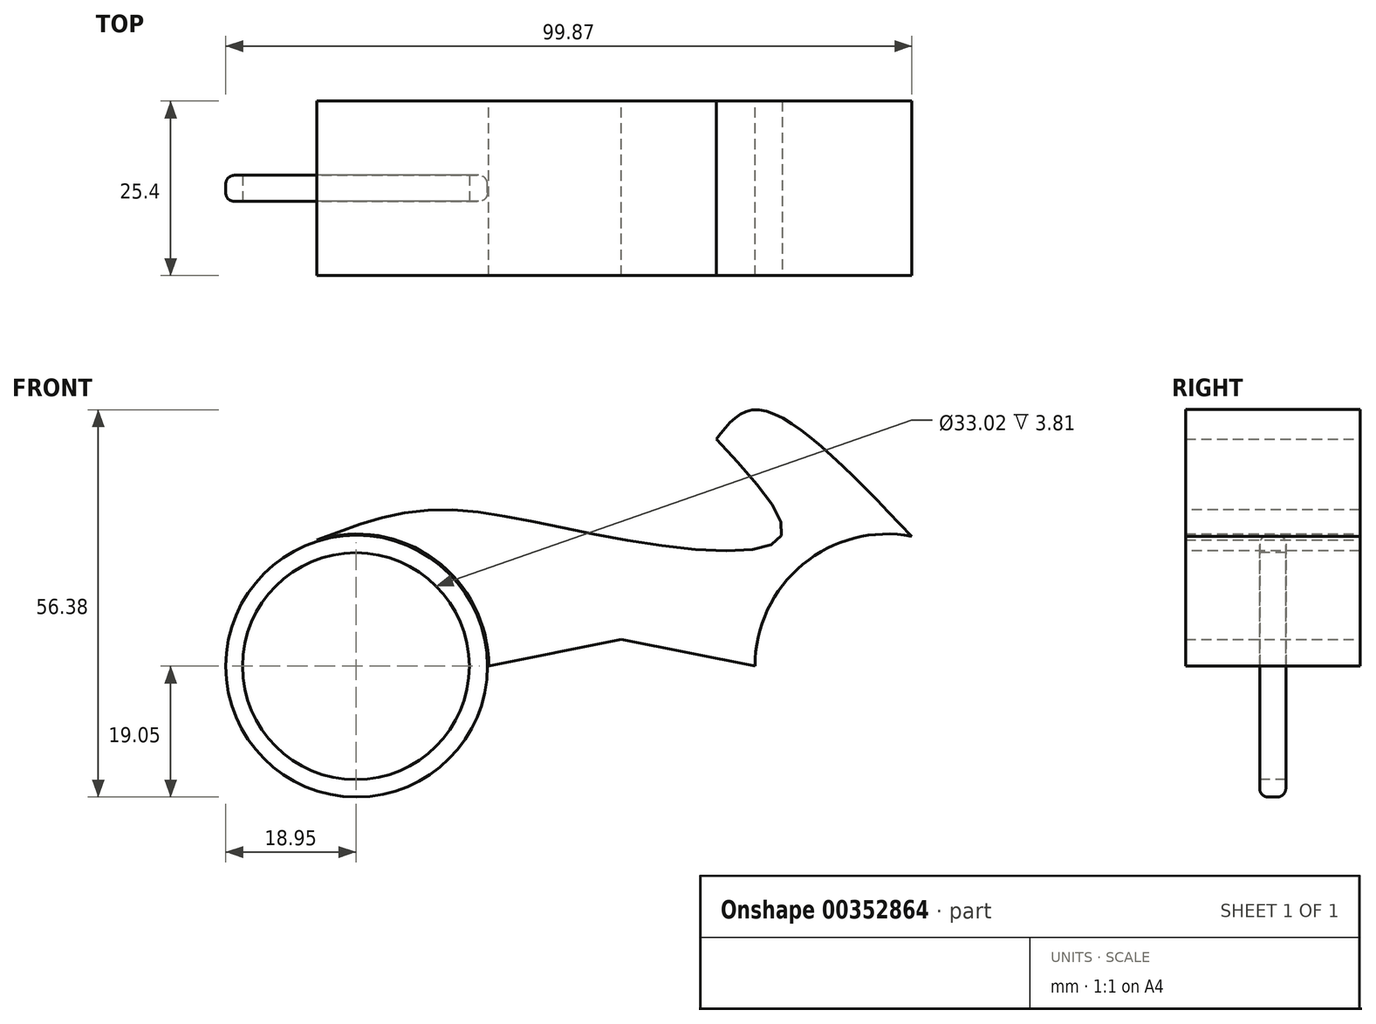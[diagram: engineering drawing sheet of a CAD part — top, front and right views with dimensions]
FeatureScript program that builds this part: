
annotation { "Feature Type Name" : "Feature", "Feature Type Description" : "" }
export const myFeature = defineFeature(function(context is Context, id is Id, definition is map)
    precondition{}
    {
        {
            var Q0;
            Q0=qCreatedBy(makeId("Front.planeOp"),FACE);
            var sketch = newSketch(context, id + "F0", { "sketchPlane" : qUnion([Q0])});
            skLineSegment(sketch, "E0", {"start": v(0, 98.93) * mm, "end": v(0, -101.88) * mm, "construction": true});
            skCircle(sketch, "E1", {"center": v(-38.52, 0) * mm, "radius": 19.05 * mm});
            skCircle(sketch, "E2.MirrorC", {"center": v(38.52, 0) * mm, "radius": 19.05 * mm});
            skSolve(sketch);
        }
        {
            var Q0;
            Q0=makeQuery(id+"F0.imprint","IMPRINT",FACE,{"disambiguationData":[TD([[makeQuery(id+"F0.imprint","IMPRINT",EDGE,{"derivedFrom":sQuery(id+"F0.wireOp",EDGE,"E1")}),1.0]])]});
            var sketch = newSketch(context, id + "F1", { "sketchPlane" : qUnion([Q0])});
            skCircle(sketch, "E3", {"center": v(38.62, 0) * mm, "radius": 16.51 * mm});
            skLineSegment(sketch, "E4", {"start": v(0, 93.6) * mm, "end": v(0, -127.2) * mm, "construction": true});
            skCircle(sketch, "E5.MirrorC", {"center": v(-38.62, 0) * mm, "radius": 16.51 * mm});
            skSolve(sketch);
        }
        {
            var Q0;
            Q0=makeQuery(id+"F0.imprint","IMPRINT",FACE,{"disambiguationData":[TD([[makeQuery(id+"F0.imprint","IMPRINT",EDGE,{"derivedFrom":sQuery(id+"F0.wireOp",EDGE,"E1")}),1.0]])]});
            var Q1;
            Q1=makeQuery(id+"F0.imprint","IMPRINT",FACE,{"disambiguationData":[TD([[makeQuery(id+"F0.imprint","IMPRINT",EDGE,{"derivedFrom":sQuery(id+"F0.wireOp",EDGE,"E2.MirrorC")}),-1.0]])]});
            extrude(context, id + "F2", {"entities" : qUnion([Q0, Q1]), "endBound" : BoundingType.SYMMETRIC, "depth" : 3.8 * mm});
        }
        {
            var Q0;
            Q0 = qSketchRegion(id + "F1", true);
            extrude(context, id + "F3", {"entities" : qUnion([Q0]), "operationType" : NewBodyOperationType.REMOVE, "endBound" : BoundingType.SYMMETRIC, "oppositeDirection" : true, "depth" : 5.08 * mm});
        }
        {
            var Q0;
            Q0=makeQuery(id+"F2.opExtrude","SWEPT_FACE",FACE,{"disambiguationData":[OSD([sQuery(id+"F0.wireOp",EDGE,"E2.MirrorC")])]});
            var Q1;
            Q1=makeQuery(id+"F2.opExtrude","SWEPT_FACE",FACE,{"disambiguationData":[OSD([sQuery(id+"F0.wireOp",EDGE,"E1")])]});
            fillet(context, id + "F4", {"entities" : qUnion([Q0, Q1]), "radius" : 1.27 * mm, "tangentPropagation" : true, "allowEdgeOverflow" : false});
        }
        {
            var Q0;
            Q0=qCreatedBy(makeId("Front.planeOp"),FACE);
            var sketch = newSketch(context, id + "F5", { "sketchPlane" : qUnion([Q0])});
            skFitSpline(sketch, "E6", {"points": [v(0, 3.92) * mm, v(19.53, 0) * mm], "startDerivative": vector(19.53, -3.92) * mm, "endDerivative": vector(19.53, -3.92) * mm});
            skFitSpline(sketch, "E7", {"points": [v(0, 3.92) * mm, v(-19.3, 0) * mm], "startDerivative": vector(-19.3, -3.92) * mm, "endDerivative": vector(-19.3, -3.92) * mm});
            skArc(sketch, "E8", {"start": v(42.3, 18.9) * mm, "mid": v(26.45, 14.82) * mm, "end": v(19.48, 0) * mm});
            skFitSpline(sketch, "E9", {"points": [v(42.3, 18.9) * mm, v(19.75, 37.33) * mm, v(13.84, 33.02) * mm], "startDerivative": vector(-39.21, 41.2) * mm, "endDerivative": vector(-15, -19.7) * mm});
            skArc(sketch, "E10", {"start": v(-19.28, 0) * mm, "mid": v(-27.14, 15.5) * mm, "end": v(-44.28, 18.35) * mm});
            skFitSpline(sketch, "E11", {"points": [v(-44.28, 18.35) * mm, v(-27.24, 22.76) * mm, v(0, 18.46) * mm, v(23.18, 18.76) * mm, v(13.84, 33.02) * mm], "startDerivative": vector(71.57, 27.63) * mm, "endDerivative": vector(-73.09, 77.35) * mm});
            skSolve(sketch);
        }
        {
            var Q0;
            {var subQ0=sQuery(id+"F5.wireOp",EDGE,"E8");Q0=makeQuery(id+"F5.imprint","IMPRINT",FACE,{"disambiguationData":[TD([[makeQuery(id+"F5.imprint","IMPRINT",EDGE,{"derivedFrom":subQ0}),-1.0]])]});}
            extrude(context, id + "F6", {"entities" : qUnion([Q0]), "operationType" : NewBodyOperationType.ADD, "endBound" : BoundingType.SYMMETRIC, "depth" : 25.4 * mm});
        }
    });
